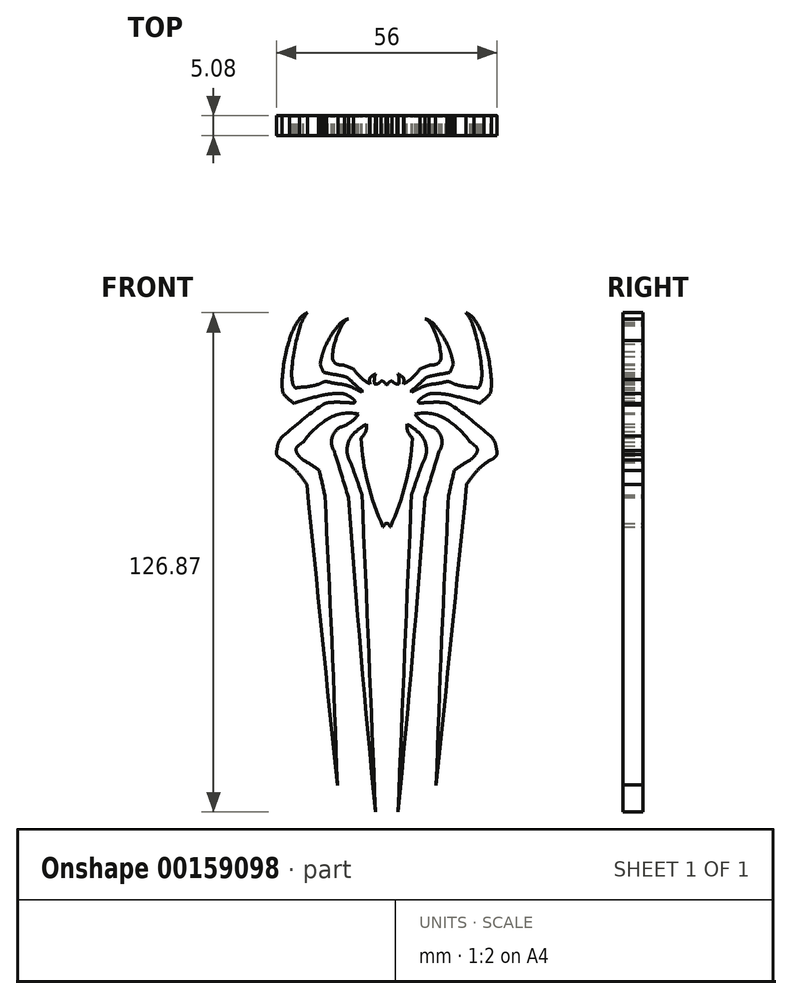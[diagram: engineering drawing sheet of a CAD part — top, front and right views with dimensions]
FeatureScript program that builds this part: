
annotation { "Feature Type Name" : "Feature", "Feature Type Description" : "" }
export const myFeature = defineFeature(function(context is Context, id is Id, definition is map)
    precondition{}
    {
        {
            var Q0;
            Q0=qCreatedBy(makeId("Front.planeOp"),FACE);
            var sketch = newSketch(context, id + "F0", { "sketchPlane" : qUnion([Q0])});
            skPoint(sketch, "E0", {"position": v(-20.2, 61.26) * mm});
            skArc(sketch, "E1", {"start": v(-20.2, 61.26) * mm, "mid": v(-21.31, 60.57) * mm, "end": v(-22.22, 59.62) * mm});
            skPoint(sketch, "E2", {"position": v(-25.42, 51.71) * mm});
            skPoint(sketch, "E3", {"position": v(-24.86, 53.92) * mm});
            skPoint(sketch, "E4", {"position": v(-24.76, 54.21) * mm});
            skArc(sketch, "E5", {"start": v(-22.22, 59.62) * mm, "mid": v(-23.72, 57.02) * mm, "end": v(-24.76, 54.21) * mm});
            skPoint(sketch, "E6", {"position": v(-26.55, 44.31) * mm});
            skArc(sketch, "E7", {"start": v(-24.76, 54.21) * mm, "mid": v(-25.96, 49.32) * mm, "end": v(-26.55, 44.31) * mm});
            skLineSegment(sketch, "E8", {"start": v(-26.55, 44.31) * mm, "end": v(-26.55, 42.46) * mm});
            skArc(sketch, "E9", {"start": v(-26.55, 42.46) * mm, "mid": v(-26.49, 41.57) * mm, "end": v(-26.3, 40.7) * mm});
            skArc(sketch, "E10", {"start": v(-26.3, 40.7) * mm, "mid": v(-25, 39.35) * mm, "end": v(-23.49, 38.23) * mm});
            skPoint(sketch, "E11", {"position": v(-13.29, 40.7) * mm});
            skPoint(sketch, "E12", {"position": v(-16.71, 40.18) * mm});
            skArc(sketch, "E13", {"start": v(-16.71, 40.18) * mm, "mid": v(-20.13, 39.3) * mm, "end": v(-23.49, 38.23) * mm});
            skArc(sketch, "E14", {"start": v(-13.29, 40.7) * mm, "mid": v(-15.01, 40.5) * mm, "end": v(-16.71, 40.18) * mm});
            skLineSegment(sketch, "E15", {"start": v(-13.29, 40.7) * mm, "end": v(-11.52, 40.7) * mm});
            skArc(sketch, "E16", {"start": v(-10.02, 40.29) * mm, "mid": v(-10.74, 40.6) * mm, "end": v(-11.52, 40.7) * mm});
            skArc(sketch, "E17", {"start": v(-8.84, 39.58) * mm, "mid": v(-9.42, 39.95) * mm, "end": v(-10.02, 40.29) * mm});
            skArc(sketch, "E18", {"start": v(-8.1, 38.82) * mm, "mid": v(-8.43, 39.24) * mm, "end": v(-8.84, 39.58) * mm});
            skArc(sketch, "E19", {"start": v(-8.25, 38.27) * mm, "mid": v(-8.1, 38.53) * mm, "end": v(-8.1, 38.82) * mm});
            skArc(sketch, "E20", {"start": v(-8.25, 38.27) * mm, "mid": v(-9.98, 38.4) * mm, "end": v(-11.72, 38.48) * mm});
            skArc(sketch, "E21", {"start": v(-11.72, 38.48) * mm, "mid": v(-13.52, 38.49) * mm, "end": v(-15.32, 38.3) * mm});
            skArc(sketch, "E22", {"start": v(-15.32, 38.3) * mm, "mid": v(-15.87, 38.08) * mm, "end": v(-16.38, 37.77) * mm});
            skArc(sketch, "E23", {"start": v(-16.38, 37.77) * mm, "mid": v(-21.47, 33.98) * mm, "end": v(-26.3, 29.87) * mm});
            skArc(sketch, "E24", {"start": v(-26.3, 29.87) * mm, "mid": v(-27.24, 28.8) * mm, "end": v(-27.72, 27.47) * mm});
            skArc(sketch, "E25", {"start": v(-27.95, 26.26) * mm, "mid": v(-27.83, 26.86) * mm, "end": v(-27.72, 27.47) * mm});
            skArc(sketch, "E26", {"start": v(-27.95, 26.26) * mm, "mid": v(-28, 25.76) * mm, "end": v(-27.95, 25.26) * mm});
            skArc(sketch, "E27", {"start": v(-27.95, 25.26) * mm, "mid": v(-27.28, 24.34) * mm, "end": v(-26.3, 23.8) * mm});
            skPoint(sketch, "E28", {"position": v(-22.96, 21.12) * mm});
            skArc(sketch, "E29", {"start": v(-22.96, 21.12) * mm, "mid": v(-24.54, 22.56) * mm, "end": v(-26.3, 23.8) * mm});
            skArc(sketch, "E30", {"start": v(-20.29, 17.6) * mm, "mid": v(-21.57, 19.4) * mm, "end": v(-22.96, 21.12) * mm});
            skArc(sketch, "E31", {"start": v(-20.29, 17.6) * mm, "mid": v(-16.45, -20.57) * mm, "end": v(-12.57, -58.74) * mm});
            skArc(sketch, "E32", {"start": v(-12.57, -58.74) * mm, "mid": v(-13.95, -21.96) * mm, "end": v(-15.73, 14.8) * mm});
            skArc(sketch, "E33", {"start": v(-15.73, 14.8) * mm, "mid": v(-16.41, 17.95) * mm, "end": v(-17.14, 21.1) * mm});
            skArc(sketch, "E34", {"start": v(-17.14, 21.1) * mm, "mid": v(-19.15, 22.56) * mm, "end": v(-21.26, 23.88) * mm});
            skArc(sketch, "E35", {"start": v(-22.27, 24.81) * mm, "mid": v(-21.8, 24.31) * mm, "end": v(-21.26, 23.88) * mm});
            skArc(sketch, "E36", {"start": v(-22.96, 25.96) * mm, "mid": v(-22.68, 25.35) * mm, "end": v(-22.27, 24.81) * mm});
            skArc(sketch, "E37", {"start": v(-22.52, 27.37) * mm, "mid": v(-22.98, 26.74) * mm, "end": v(-22.96, 25.96) * mm});
            skArc(sketch, "E38", {"start": v(-21.17, 28.4) * mm, "mid": v(-21.86, 27.9) * mm, "end": v(-22.52, 27.37) * mm});
            skArc(sketch, "E39", {"start": v(-15.23, 34.08) * mm, "mid": v(-18.48, 31.53) * mm, "end": v(-21.17, 28.4) * mm});
            skArc(sketch, "E40", {"start": v(-7.23, 35.47) * mm, "mid": v(-11.37, 35.57) * mm, "end": v(-15.23, 34.08) * mm});
            skArc(sketch, "E41", {"start": v(-11.54, 32.26) * mm, "mid": v(-9.1, 33.48) * mm, "end": v(-7.23, 35.47) * mm});
            skArc(sketch, "E42", {"start": v(-11.54, 32.26) * mm, "mid": v(-13.88, 29.54) * mm, "end": v(-13.3, 26) * mm});
            skArc(sketch, "E43", {"start": v(-9.74, 14.25) * mm, "mid": v(-11.51, 20.12) * mm, "end": v(-13.3, 26) * mm});
            skArc(sketch, "E44", {"start": v(-9.74, 14.25) * mm, "mid": v(-6.54, -25.7) * mm, "end": v(-2.88, -65.61) * mm});
            skArc(sketch, "E45", {"start": v(-2.88, -65.61) * mm, "mid": v(-4.54, -25.3) * mm, "end": v(-6.3, 15) * mm});
            skArc(sketch, "E46", {"start": v(-6.3, 15) * mm, "mid": v(-7.72, 19.07) * mm, "end": v(-9.16, 23.13) * mm});
            skArc(sketch, "E47", {"start": v(-7.68, 31.1) * mm, "mid": v(-10.01, 27.41) * mm, "end": v(-9.16, 23.13) * mm});
            skArc(sketch, "E48", {"start": v(-5.15, 32.91) * mm, "mid": v(-6.49, 32.11) * mm, "end": v(-7.68, 31.1) * mm});
            skArc(sketch, "E49", {"start": v(-6.57, 29.36) * mm, "mid": v(-5.4, 30.95) * mm, "end": v(-5.15, 32.91) * mm});
            skArc(sketch, "E50", {"start": v(-6.57, 29.36) * mm, "mid": v(-4.8, 17.81) * mm, "end": v(-0.9, 6.8) * mm});
            skArc(sketch, "E51", {"start": v(-0.35, 7.66) * mm, "mid": v(-0.64, 7.24) * mm, "end": v(-0.9, 6.8) * mm});
            skArc(sketch, "E52", {"start": v(0, 7.66) * mm, "mid": v(-0.18, 7.68) * mm, "end": v(-0.35, 7.66) * mm});
            skArc(sketch, "E53", {"start": v(-20.2, 61.26) * mm, "mid": v(-21.14, 59.83) * mm, "end": v(-21.84, 58.25) * mm});
            skArc(sketch, "E54", {"start": v(-21.84, 58.25) * mm, "mid": v(-23.31, 52.58) * mm, "end": v(-24.12, 46.78) * mm});
            skArc(sketch, "E55", {"start": v(-24.12, 46.78) * mm, "mid": v(-24.13, 45.05) * mm, "end": v(-23.9, 43.34) * mm});
            skArc(sketch, "E56", {"start": v(-23.9, 43.34) * mm, "mid": v(-23.68, 42.72) * mm, "end": v(-23.28, 42.18) * mm});
            skArc(sketch, "E57", {"start": v(-23.28, 42.18) * mm, "mid": v(-22.96, 42.12) * mm, "end": v(-22.68, 42.3) * mm});
            skArc(sketch, "E58", {"start": v(-22.68, 42.3) * mm, "mid": v(-19.98, 42.45) * mm, "end": v(-17.34, 43.03) * mm});
            skArc(sketch, "E59", {"start": v(-17.34, 43.03) * mm, "mid": v(-16.71, 43.35) * mm, "end": v(-16.09, 43.67) * mm});
            skArc(sketch, "E60", {"start": v(-14.86, 43.67) * mm, "mid": v(-15.47, 43.7) * mm, "end": v(-16.09, 43.67) * mm});
            skArc(sketch, "E61", {"start": v(-14.86, 43.67) * mm, "mid": v(-13.37, 43.32) * mm, "end": v(-11.85, 43.13) * mm});
            skArc(sketch, "E62", {"start": v(-8.81, 42.3) * mm, "mid": v(-10.3, 42.8) * mm, "end": v(-11.85, 43.13) * mm});
            skArc(sketch, "E63", {"start": v(-8.81, 42.3) * mm, "mid": v(-7.54, 41.64) * mm, "end": v(-6.25, 41.02) * mm});
            skArc(sketch, "E64", {"start": v(-6.25, 41.6) * mm, "mid": v(-6.26, 41.3) * mm, "end": v(-6.25, 41.02) * mm});
            skArc(sketch, "E65", {"start": v(-7.32, 42.26) * mm, "mid": v(-6.82, 41.87) * mm, "end": v(-6.25, 41.6) * mm});
            skArc(sketch, "E66", {"start": v(-9.76, 44.6) * mm, "mid": v(-8.55, 43.42) * mm, "end": v(-7.32, 42.26) * mm});
            skArc(sketch, "E67", {"start": v(-9.76, 44.6) * mm, "mid": v(-10.41, 44.9) * mm, "end": v(-11.1, 45.12) * mm});
            skArc(sketch, "E68", {"start": v(-16.03, 46.09) * mm, "mid": v(-13.57, 45.6) * mm, "end": v(-11.1, 45.12) * mm});
            skArc(sketch, "E69", {"start": v(-16.9, 48.27) * mm, "mid": v(-16.53, 47.15) * mm, "end": v(-16.03, 46.09) * mm});
            skArc(sketch, "E70", {"start": v(-16.12, 51.43) * mm, "mid": v(-16.55, 49.86) * mm, "end": v(-16.9, 48.27) * mm});
            skArc(sketch, "E71", {"start": v(-15.3, 53.3) * mm, "mid": v(-15.75, 52.38) * mm, "end": v(-16.12, 51.43) * mm});
            skArc(sketch, "E72", {"start": v(-12.35, 57.93) * mm, "mid": v(-13.97, 55.71) * mm, "end": v(-15.3, 53.3) * mm});
            skArc(sketch, "E73", {"start": v(-10.71, 59.32) * mm, "mid": v(-11.6, 58.71) * mm, "end": v(-12.35, 57.93) * mm});
            skArc(sketch, "E74", {"start": v(-9.66, 59.66) * mm, "mid": v(-10.2, 59.55) * mm, "end": v(-10.71, 59.32) * mm});
            skArc(sketch, "E75", {"start": v(-9.66, 59.66) * mm, "mid": v(-10.35, 59.34) * mm, "end": v(-10.9, 58.8) * mm});
            skArc(sketch, "E76", {"start": v(-10.9, 58.8) * mm, "mid": v(-12.9, 54.64) * mm, "end": v(-13.79, 50.1) * mm});
            skArc(sketch, "E77", {"start": v(-13.79, 50.1) * mm, "mid": v(-13.3, 48.63) * mm, "end": v(-11.88, 48) * mm});
            skArc(sketch, "E78", {"start": v(-11.1, 48) * mm, "mid": v(-11.49, 48) * mm, "end": v(-11.88, 48) * mm});
            skArc(sketch, "E79", {"start": v(-8.45, 46.95) * mm, "mid": v(-9.76, 47.5) * mm, "end": v(-11.1, 48) * mm});
            skArc(sketch, "E80", {"start": v(-8.45, 46.95) * mm, "mid": v(-7.35, 45.59) * mm, "end": v(-6.1, 44.36) * mm});
            skArc(sketch, "E81", {"start": v(-6.1, 44.36) * mm, "mid": v(-5.2, 43.68) * mm, "end": v(-4.22, 43.14) * mm});
            skArc(sketch, "E82", {"start": v(-4.26, 44.74) * mm, "mid": v(-4.34, 43.94) * mm, "end": v(-4.22, 43.14) * mm});
            skArc(sketch, "E83", {"start": v(-2.85, 45.67) * mm, "mid": v(-3.6, 45.26) * mm, "end": v(-4.26, 44.74) * mm});
            skArc(sketch, "E84", {"start": v(-2.85, 45.67) * mm, "mid": v(-3.08, 45.02) * mm, "end": v(-3.16, 44.34) * mm});
            skArc(sketch, "E85", {"start": v(-3.16, 44.34) * mm, "mid": v(-3.17, 43.85) * mm, "end": v(-3.16, 43.35) * mm});
            skArc(sketch, "E86", {"start": v(-3.16, 43.35) * mm, "mid": v(-2.96, 43.1) * mm, "end": v(-2.63, 43.1) * mm});
            skArc(sketch, "E87", {"start": v(-2.63, 43.1) * mm, "mid": v(-1.95, 43.39) * mm, "end": v(-1.4, 43.88) * mm});
            skArc(sketch, "E88", {"start": v(-0.2, 42.94) * mm, "mid": v(-0.64, 43.62) * mm, "end": v(-1.4, 43.88) * mm});
            skArc(sketch, "E89", {"start": v(0, 42.94) * mm, "mid": v(-0.1, 42.94) * mm, "end": v(-0.2, 42.94) * mm});
            skArc(sketch, "E90.MirrorCS", {"start": v(6.57, 29.36) * mm, "mid": v(4.8, 17.81) * mm, "end": v(0.9, 6.8) * mm});
            skArc(sketch, "E91.MirrorCS", {"start": v(0.35, 7.66) * mm, "mid": v(0.64, 7.24) * mm, "end": v(0.9, 6.8) * mm});
            skArc(sketch, "E92.MirrorCS", {"start": v(0, 7.66) * mm, "mid": v(0.18, 7.68) * mm, "end": v(0.35, 7.66) * mm});
            skArc(sketch, "E93.MirrorCS", {"start": v(6.57, 29.36) * mm, "mid": v(5.4, 30.95) * mm, "end": v(5.15, 32.91) * mm});
            skArc(sketch, "E94.MirrorCS", {"start": v(5.15, 32.91) * mm, "mid": v(6.49, 32.11) * mm, "end": v(7.68, 31.1) * mm});
            skArc(sketch, "E95.MirrorCS", {"start": v(7.68, 31.1) * mm, "mid": v(10.01, 27.41) * mm, "end": v(9.16, 23.13) * mm});
            skArc(sketch, "E96.MirrorCS", {"start": v(6.3, 15) * mm, "mid": v(7.72, 19.07) * mm, "end": v(9.16, 23.13) * mm});
            skArc(sketch, "E97.MirrorCS", {"start": v(2.88, -65.61) * mm, "mid": v(4.54, -25.3) * mm, "end": v(6.3, 15) * mm});
            skArc(sketch, "E98.MirrorCS", {"start": v(9.74, 14.25) * mm, "mid": v(6.54, -25.7) * mm, "end": v(2.88, -65.61) * mm});
            skArc(sketch, "E99.MirrorCS", {"start": v(9.74, 14.25) * mm, "mid": v(11.51, 20.12) * mm, "end": v(13.3, 26) * mm});
            skArc(sketch, "E100.MirrorCS", {"start": v(11.54, 32.26) * mm, "mid": v(13.88, 29.54) * mm, "end": v(13.3, 26) * mm});
            skArc(sketch, "E101.MirrorCS", {"start": v(11.54, 32.26) * mm, "mid": v(9.1, 33.48) * mm, "end": v(7.23, 35.47) * mm});
            skArc(sketch, "E102.MirrorCS", {"start": v(7.23, 35.47) * mm, "mid": v(11.37, 35.57) * mm, "end": v(15.23, 34.08) * mm});
            skArc(sketch, "E103.MirrorCS", {"start": v(15.23, 34.08) * mm, "mid": v(18.48, 31.53) * mm, "end": v(21.17, 28.4) * mm});
            skArc(sketch, "E104.MirrorCS", {"start": v(21.17, 28.4) * mm, "mid": v(21.86, 27.9) * mm, "end": v(22.52, 27.37) * mm});
            skArc(sketch, "E105.MirrorCS", {"start": v(22.52, 27.37) * mm, "mid": v(22.98, 26.74) * mm, "end": v(22.96, 25.96) * mm});
            skArc(sketch, "E106.MirrorCS", {"start": v(22.96, 25.96) * mm, "mid": v(22.68, 25.35) * mm, "end": v(22.27, 24.81) * mm});
            skArc(sketch, "E107.MirrorCS", {"start": v(22.27, 24.81) * mm, "mid": v(21.8, 24.31) * mm, "end": v(21.26, 23.88) * mm});
            skArc(sketch, "E108.MirrorCS", {"start": v(17.14, 21.1) * mm, "mid": v(19.15, 22.56) * mm, "end": v(21.26, 23.88) * mm});
            skArc(sketch, "E109.MirrorCS", {"start": v(15.73, 14.8) * mm, "mid": v(16.41, 17.95) * mm, "end": v(17.14, 21.1) * mm});
            skArc(sketch, "E110.MirrorCS", {"start": v(12.57, -58.74) * mm, "mid": v(13.95, -21.96) * mm, "end": v(15.73, 14.8) * mm});
            skArc(sketch, "E111.MirrorCS", {"start": v(20.29, 17.6) * mm, "mid": v(16.45, -20.57) * mm, "end": v(12.57, -58.74) * mm});
            skArc(sketch, "E112.MirrorCS", {"start": v(20.29, 17.6) * mm, "mid": v(21.57, 19.4) * mm, "end": v(22.96, 21.12) * mm});
            skArc(sketch, "E113.MirrorCS", {"start": v(22.96, 21.12) * mm, "mid": v(24.54, 22.56) * mm, "end": v(26.3, 23.8) * mm});
            skArc(sketch, "E114.MirrorCS", {"start": v(27.95, 25.26) * mm, "mid": v(27.28, 24.34) * mm, "end": v(26.3, 23.8) * mm});
            skArc(sketch, "E115.MirrorCS", {"start": v(27.95, 26.26) * mm, "mid": v(28, 25.76) * mm, "end": v(27.95, 25.26) * mm});
            skArc(sketch, "E116.MirrorCS", {"start": v(27.95, 26.26) * mm, "mid": v(27.83, 26.86) * mm, "end": v(27.72, 27.47) * mm});
            skArc(sketch, "E117.MirrorCS", {"start": v(26.3, 29.87) * mm, "mid": v(27.24, 28.8) * mm, "end": v(27.72, 27.47) * mm});
            skArc(sketch, "E118.MirrorCS", {"start": v(16.38, 37.77) * mm, "mid": v(21.47, 33.98) * mm, "end": v(26.3, 29.87) * mm});
            skArc(sketch, "E119.MirrorCS", {"start": v(11.72, 38.48) * mm, "mid": v(13.52, 38.49) * mm, "end": v(15.32, 38.3) * mm});
            skArc(sketch, "E120.MirrorCS", {"start": v(15.32, 38.3) * mm, "mid": v(15.87, 38.08) * mm, "end": v(16.38, 37.77) * mm});
            skArc(sketch, "E121.MirrorCS", {"start": v(8.25, 38.27) * mm, "mid": v(9.98, 38.4) * mm, "end": v(11.72, 38.48) * mm});
            skArc(sketch, "E122.MirrorCS", {"start": v(8.25, 38.27) * mm, "mid": v(8.1, 38.53) * mm, "end": v(8.1, 38.82) * mm});
            skArc(sketch, "E123.MirrorCS", {"start": v(8.1, 38.82) * mm, "mid": v(8.43, 39.24) * mm, "end": v(8.84, 39.58) * mm});
            skArc(sketch, "E124.MirrorCS", {"start": v(8.84, 39.58) * mm, "mid": v(9.42, 39.95) * mm, "end": v(10.02, 40.29) * mm});
            skArc(sketch, "E125.MirrorCS", {"start": v(10.02, 40.29) * mm, "mid": v(10.74, 40.6) * mm, "end": v(11.52, 40.7) * mm});
            skLineSegment(sketch, "E126.MirrorCS", {"start": v(13.29, 40.7) * mm, "end": v(11.52, 40.7) * mm});
            skArc(sketch, "E127.MirrorCS", {"start": v(13.29, 40.7) * mm, "mid": v(15.01, 40.5) * mm, "end": v(16.71, 40.18) * mm});
            skArc(sketch, "E128.MirrorCS", {"start": v(16.71, 40.18) * mm, "mid": v(20.13, 39.3) * mm, "end": v(23.49, 38.23) * mm});
            skArc(sketch, "E129.MirrorCS", {"start": v(26.3, 40.7) * mm, "mid": v(25, 39.35) * mm, "end": v(23.49, 38.23) * mm});
            skArc(sketch, "E130.MirrorCS", {"start": v(26.55, 42.46) * mm, "mid": v(26.49, 41.57) * mm, "end": v(26.3, 40.7) * mm});
            skLineSegment(sketch, "E131.MirrorCS", {"start": v(26.55, 44.31) * mm, "end": v(26.55, 42.46) * mm});
            skArc(sketch, "E132.MirrorCS", {"start": v(24.76, 54.21) * mm, "mid": v(25.96, 49.32) * mm, "end": v(26.55, 44.31) * mm});
            skArc(sketch, "E133.MirrorCS", {"start": v(21.84, 58.25) * mm, "mid": v(23.31, 52.58) * mm, "end": v(24.12, 46.78) * mm});
            skArc(sketch, "E134.MirrorCS", {"start": v(24.12, 46.78) * mm, "mid": v(24.13, 45.05) * mm, "end": v(23.9, 43.34) * mm});
            skArc(sketch, "E135.MirrorCS", {"start": v(22.22, 59.62) * mm, "mid": v(23.72, 57.02) * mm, "end": v(24.76, 54.21) * mm});
            skArc(sketch, "E136.MirrorCS", {"start": v(20.2, 61.26) * mm, "mid": v(21.14, 59.83) * mm, "end": v(21.84, 58.25) * mm});
            skArc(sketch, "E137.MirrorCS", {"start": v(20.2, 61.26) * mm, "mid": v(21.31, 60.57) * mm, "end": v(22.22, 59.62) * mm});
            skArc(sketch, "E138.MirrorCS", {"start": v(22.68, 42.3) * mm, "mid": v(19.98, 42.45) * mm, "end": v(17.34, 43.03) * mm});
            skArc(sketch, "E139.MirrorCS", {"start": v(14.86, 43.67) * mm, "mid": v(13.37, 43.32) * mm, "end": v(11.85, 43.13) * mm});
            skArc(sketch, "E140.MirrorCS", {"start": v(23.9, 43.34) * mm, "mid": v(23.68, 42.72) * mm, "end": v(23.28, 42.18) * mm});
            skArc(sketch, "E141.MirrorCS", {"start": v(23.28, 42.18) * mm, "mid": v(22.96, 42.12) * mm, "end": v(22.68, 42.3) * mm});
            skArc(sketch, "E142.MirrorCS", {"start": v(17.34, 43.03) * mm, "mid": v(16.71, 43.35) * mm, "end": v(16.09, 43.67) * mm});
            skArc(sketch, "E143.MirrorCS", {"start": v(14.86, 43.67) * mm, "mid": v(15.47, 43.7) * mm, "end": v(16.09, 43.67) * mm});
            skArc(sketch, "E144.MirrorCS", {"start": v(8.81, 42.3) * mm, "mid": v(10.3, 42.8) * mm, "end": v(11.85, 43.13) * mm});
            skArc(sketch, "E145.MirrorCS", {"start": v(8.81, 42.3) * mm, "mid": v(7.54, 41.64) * mm, "end": v(6.25, 41.02) * mm});
            skArc(sketch, "E146.MirrorCS", {"start": v(6.25, 41.6) * mm, "mid": v(6.26, 41.3) * mm, "end": v(6.25, 41.02) * mm});
            skArc(sketch, "E147.MirrorCS", {"start": v(7.32, 42.26) * mm, "mid": v(6.82, 41.87) * mm, "end": v(6.25, 41.6) * mm});
            skArc(sketch, "E148.MirrorCS", {"start": v(9.76, 44.6) * mm, "mid": v(8.55, 43.42) * mm, "end": v(7.32, 42.26) * mm});
            skArc(sketch, "E149.MirrorCS", {"start": v(9.76, 44.6) * mm, "mid": v(10.41, 44.9) * mm, "end": v(11.1, 45.12) * mm});
            skArc(sketch, "E150.MirrorCS", {"start": v(16.03, 46.09) * mm, "mid": v(13.57, 45.6) * mm, "end": v(11.1, 45.12) * mm});
            skArc(sketch, "E151.MirrorCS", {"start": v(16.9, 48.27) * mm, "mid": v(16.53, 47.15) * mm, "end": v(16.03, 46.09) * mm});
            skArc(sketch, "E152.MirrorCS", {"start": v(16.12, 51.43) * mm, "mid": v(16.55, 49.86) * mm, "end": v(16.9, 48.27) * mm});
            skArc(sketch, "E153.MirrorCS", {"start": v(15.3, 53.3) * mm, "mid": v(15.75, 52.38) * mm, "end": v(16.12, 51.43) * mm});
            skArc(sketch, "E154.MirrorCS", {"start": v(12.35, 57.93) * mm, "mid": v(13.97, 55.71) * mm, "end": v(15.3, 53.3) * mm});
            skArc(sketch, "E155.MirrorCS", {"start": v(10.71, 59.32) * mm, "mid": v(11.6, 58.71) * mm, "end": v(12.35, 57.93) * mm});
            skArc(sketch, "E156.MirrorCS", {"start": v(9.66, 59.66) * mm, "mid": v(10.2, 59.55) * mm, "end": v(10.71, 59.32) * mm});
            skArc(sketch, "E157.MirrorCS", {"start": v(9.66, 59.66) * mm, "mid": v(10.35, 59.34) * mm, "end": v(10.9, 58.8) * mm});
            skArc(sketch, "E158.MirrorCS", {"start": v(10.9, 58.8) * mm, "mid": v(12.9, 54.64) * mm, "end": v(13.79, 50.1) * mm});
            skArc(sketch, "E159.MirrorCS", {"start": v(13.79, 50.1) * mm, "mid": v(13.3, 48.63) * mm, "end": v(11.88, 48) * mm});
            skArc(sketch, "E160.MirrorCS", {"start": v(11.1, 48) * mm, "mid": v(11.49, 48) * mm, "end": v(11.88, 48) * mm});
            skArc(sketch, "E161.MirrorCS", {"start": v(8.45, 46.95) * mm, "mid": v(9.76, 47.5) * mm, "end": v(11.1, 48) * mm});
            skArc(sketch, "E162.MirrorCS", {"start": v(8.45, 46.95) * mm, "mid": v(7.35, 45.59) * mm, "end": v(6.1, 44.36) * mm});
            skArc(sketch, "E163.MirrorCS", {"start": v(6.1, 44.36) * mm, "mid": v(5.2, 43.68) * mm, "end": v(4.22, 43.14) * mm});
            skArc(sketch, "E164.MirrorCS", {"start": v(4.26, 44.74) * mm, "mid": v(4.34, 43.94) * mm, "end": v(4.22, 43.14) * mm});
            skArc(sketch, "E165.MirrorCS", {"start": v(2.85, 45.67) * mm, "mid": v(3.6, 45.26) * mm, "end": v(4.26, 44.74) * mm});
            skArc(sketch, "E166.MirrorCS", {"start": v(2.85, 45.67) * mm, "mid": v(3.08, 45.02) * mm, "end": v(3.16, 44.34) * mm});
            skArc(sketch, "E167.MirrorCS", {"start": v(3.16, 44.34) * mm, "mid": v(3.17, 43.85) * mm, "end": v(3.16, 43.35) * mm});
            skArc(sketch, "E168.MirrorCS", {"start": v(3.16, 43.35) * mm, "mid": v(2.96, 43.1) * mm, "end": v(2.63, 43.1) * mm});
            skArc(sketch, "E169.MirrorCS", {"start": v(2.63, 43.1) * mm, "mid": v(1.95, 43.39) * mm, "end": v(1.4, 43.88) * mm});
            skArc(sketch, "E170.MirrorCS", {"start": v(0.2, 42.94) * mm, "mid": v(0.64, 43.62) * mm, "end": v(1.4, 43.88) * mm});
            skArc(sketch, "E171.MirrorCS", {"start": v(0, 42.94) * mm, "mid": v(0.1, 42.94) * mm, "end": v(0.2, 42.94) * mm});
            skSolve(sketch);
        }
        {
            var Q0;
            Q0=makeQuery(id+"F0.imprint","IMPRINT",FACE,{"disambiguationData":[TD([[makeQuery(id+"F0.imprint","IMPRINT",EDGE,{"derivedFrom":sQuery(id+"F0.wireOp",EDGE,"E1")}),1.0]])]});
            extrude(context, id + "F1", {"entities" : qUnion([Q0]), "endBound" : BoundingType.SYMMETRIC, "depth" : 5.08 * mm});
        }
    });
